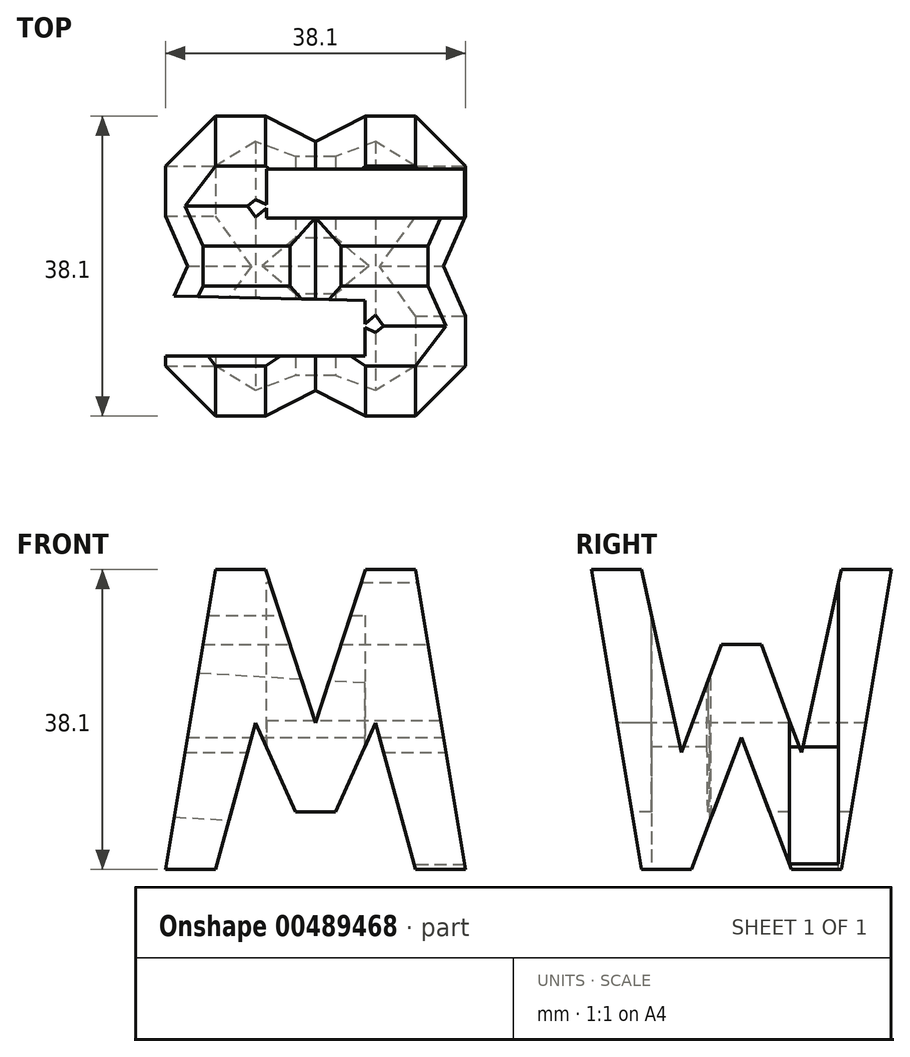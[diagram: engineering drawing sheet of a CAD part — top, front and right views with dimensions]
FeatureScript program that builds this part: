
annotation { "Feature Type Name" : "Feature", "Feature Type Description" : "" }
export const myFeature = defineFeature(function(context is Context, id is Id, definition is map)
    precondition{}
    {
        {
            var Q0;
            Q0=qCreatedBy(makeId("Front.planeOp"),FACE);
            var sketch = newSketch(context, id + "F0", { "sketchPlane" : qUnion([Q0])});
            skLineSegment(sketch, "E0", {"start": v(0, 0) * mm, "end": v(38.1, 0) * mm});
            skLineSegment(sketch, "E1", {"start": v(38.1, 0) * mm, "end": v(38.1, 38.1) * mm});
            skLineSegment(sketch, "E2", {"start": v(38.1, 38.1) * mm, "end": v(0, 38.1) * mm});
            skLineSegment(sketch, "E3", {"start": v(0, 38.1) * mm, "end": v(0, 0) * mm});
            skSolve(sketch);
        }
        {
            var Q0;
            Q0=makeQuery(id+"F0.imprint","IMPRINT",FACE,{"disambiguationData":[TD([[makeQuery(id+"F0.imprint","IMPRINT",EDGE,{"derivedFrom":sQuery(id+"F0.wireOp",EDGE,"E0")}),1.0]])]});
            extrude(context, id + "F1", {"entities" : qUnion([Q0]), "depth" : 38.1 * mm, "offsetDistance" : 25.4 * mm});
        }
        {
            var Q0;
            Q0=qCreatedBy(makeId("Front.planeOp"),FACE);
            cPlane(context, id + "F2", {"entities" : qUnion([Q0]), "cplaneType" : CPlaneType.OFFSET, "offset" : 38.1 * mm, "width" : 152.4 * mm, "height" : 152.4 * mm});
        }
        {
            var Q0;
            Q0=qCreatedBy(makeId("Right.planeOp"),FACE);
            cPlane(context, id + "F3", {"entities" : qUnion([Q0]), "cplaneType" : CPlaneType.OFFSET, "offset" : 38.1 * mm, "width" : 152.4 * mm, "height" : 152.4 * mm});
        }
        {
            var Q0;
            Q0=qCreatedBy(makeId("Top.planeOp"),FACE);
            cPlane(context, id + "F4", {"entities" : qUnion([Q0]), "cplaneType" : CPlaneType.OFFSET, "offset" : 38.1 * mm, "width" : 152.4 * mm, "height" : 152.4 * mm});
        }
        {
            var Q0;
            Q0=qCreatedBy(id+"F3.planeOp",FACE);
            var sketch = newSketch(context, id + "F5", { "sketchPlane" : qUnion([Q0])});
            skLineSegment(sketch, "E4", {"start": v(-38.1, 0) * mm, "end": v(0, 0) * mm});
            skLineSegment(sketch, "E5", {"start": v(0, 0) * mm, "end": v(0, 38.1) * mm});
            skLineSegment(sketch, "E6", {"start": v(-38.1, 0) * mm, "end": v(-38.1, 38.1) * mm});
            skLineSegment(sketch, "E7", {"start": v(-38.1, 38.1) * mm, "end": v(0, 38.1) * mm});
            skLineSegment(sketch, "E8", {"start": v(-38.1, 38.1) * mm, "end": v(-31.75, 0) * mm});
            skLineSegment(sketch, "E9", {"start": v(-31.75, 38.1) * mm, "end": v(-26.67, 14.84) * mm});
            skLineSegment(sketch, "E10", {"start": v(-26.67, 14.84) * mm, "end": v(-21.59, 28.58) * mm});
            skLineSegment(sketch, "E11", {"start": v(-21.59, 28.58) * mm, "end": v(-16.5, 28.58) * mm});
            skLineSegment(sketch, "E12", {"start": v(-16.5, 28.58) * mm, "end": v(-11.43, 14.84) * mm});
            skLineSegment(sketch, "E13", {"start": v(-11.43, 14.84) * mm, "end": v(-6.35, 38.1) * mm});
            skPoint(sketch, "E14.end.orphan", {"position": v(-6.35, 2.22) * mm});
            skLineSegment(sketch, "E15", {"start": v(0, 38.1) * mm, "end": v(-6.35, 0) * mm});
            skPoint(sketch, "E16.end.orphan", {"position": v(-17.5, 15.88) * mm});
            skPoint(sketch, "E17.endSnap0", {"position": v(-19.05, 0) * mm});
            skLineSegment(sketch, "E18", {"start": v(-19.05, 16.79) * mm, "end": v(-12.7, 0) * mm});
            skLineSegment(sketch, "E19", {"start": v(-19.05, 16.79) * mm, "end": v(-25.4, 0) * mm});
            skLineSegment(sketch, "E20.bottom", {"start": v(0, 0) * mm, "end": v(-38.1, 0) * mm});
            skLineSegment(sketch, "E20.top", {"start": v(0, 38.1) * mm, "end": v(-38.1, 38.1) * mm});
            skSolve(sketch);
        }
        {
            var Q0;
            {var subQ1=sQuery(id+"F5.wireOp",EDGE,"E9");Q0=makeQuery(id+"F5.imprint","IMPRINT",FACE,{"disambiguationData":[TD([[makeQuery(id+"F5.imprint","IMPRINT",EDGE,{"derivedFrom":subQ1}),1.0]])]});}
            var Q1;
            {var subQ0=sQuery(id+"F5.wireOp",EDGE,"E8");Q1=makeQuery(id+"F5.imprint","IMPRINT",FACE,{"disambiguationData":[TD([[makeQuery(id+"F5.imprint","IMPRINT",EDGE,{"derivedFrom":subQ0}),-1.0]])]});}
            var Q2;
            {var subQ0=sQuery(id+"F5.wireOp",EDGE,"E18");Q2=makeQuery(id+"F5.imprint","IMPRINT",FACE,{"disambiguationData":[TD([[makeQuery(id+"F5.imprint","IMPRINT",EDGE,{"derivedFrom":subQ0}),-1.0]])]});}
            var Q3;
            {var subQ0=sQuery(id+"F5.wireOp",EDGE,"E15");Q3=makeQuery(id+"F5.imprint","IMPRINT",FACE,{"disambiguationData":[TD([[makeQuery(id+"F5.imprint","IMPRINT",EDGE,{"derivedFrom":subQ0}),1.0]])]});}
            extrude(context, id + "F6", {"entities" : qUnion([Q0, Q1, Q2, Q3]), "operationType" : NewBodyOperationType.REMOVE, "oppositeDirection" : true, "depth" : 38.1 * mm, "offsetDistance" : 25.4 * mm});
        }
        {
            var Q0;
            Q0=qCreatedBy(id+"F2.planeOp",FACE);
            var sketch = newSketch(context, id + "F7", { "sketchPlane" : qUnion([Q0])});
            skLineSegment(sketch, "E21", {"start": v(0, 0) * mm, "end": v(0, 38.1) * mm});
            skLineSegment(sketch, "E22", {"start": v(0, 38.1) * mm, "end": v(38.1, 38.1) * mm});
            skLineSegment(sketch, "E23", {"start": v(38.1, 38.1) * mm, "end": v(38.1, 0) * mm});
            skLineSegment(sketch, "E24", {"start": v(38.1, 0) * mm, "end": v(0, 0) * mm});
            skLineSegment(sketch, "E25", {"start": v(6.35, 38.1) * mm, "end": v(0, 0) * mm});
            skLineSegment(sketch, "E26", {"start": v(12.7, 38.1) * mm, "end": v(19.05, 18.62) * mm});
            skLineSegment(sketch, "E27", {"start": v(19.05, 18.62) * mm, "end": v(25.4, 38.1) * mm});
            skLineSegment(sketch, "E28", {"start": v(31.75, 38.1) * mm, "end": v(38.1, 0) * mm});
            skLineSegment(sketch, "E29", {"start": v(31.75, 0) * mm, "end": v(26.67, 18.62) * mm});
            skLineSegment(sketch, "E30", {"start": v(26.67, 18.62) * mm, "end": v(21.6, 7.31) * mm});
            skLineSegment(sketch, "E31", {"start": v(21.6, 7.31) * mm, "end": v(16.51, 7.31) * mm});
            skLineSegment(sketch, "E32", {"start": v(16.51, 7.31) * mm, "end": v(11.43, 18.62) * mm});
            skLineSegment(sketch, "E33", {"start": v(11.43, 18.62) * mm, "end": v(6.35, 0) * mm});
            skSolve(sketch);
        }
        {
            var Q0;
            {var subQ0=sQuery(id+"F7.wireOp",EDGE,"E26");Q0=makeQuery(id+"F7.imprint","IMPRINT",FACE,{"disambiguationData":[TD([[makeQuery(id+"F7.imprint","IMPRINT",EDGE,{"derivedFrom":subQ0}),1.0]])]});}
            var Q1;
            {var subQ0=sQuery(id+"F7.wireOp",EDGE,"E21");Q1=makeQuery(id+"F7.imprint","IMPRINT",FACE,{"disambiguationData":[TD([[makeQuery(id+"F7.imprint","IMPRINT",EDGE,{"derivedFrom":subQ0}),-1.0]])]});}
            var Q2;
            {var subQ0=sQuery(id+"F7.wireOp",EDGE,"E29");Q2=makeQuery(id+"F7.imprint","IMPRINT",FACE,{"disambiguationData":[TD([[makeQuery(id+"F7.imprint","IMPRINT",EDGE,{"derivedFrom":subQ0}),1.0]])]});}
            var Q3;
            {var subQ0=sQuery(id+"F7.wireOp",EDGE,"E23");Q3=makeQuery(id+"F7.imprint","IMPRINT",FACE,{"disambiguationData":[TD([[makeQuery(id+"F7.imprint","IMPRINT",EDGE,{"derivedFrom":subQ0}),-1.0]])]});}
            extrude(context, id + "F8", {"entities" : qUnion([Q0, Q1, Q2, Q3]), "operationType" : NewBodyOperationType.REMOVE, "oppositeDirection" : true, "depth" : 38.1 * mm, "offsetDistance" : 25.4 * mm});
        }
        {
            var Q0;
            Q0=qCreatedBy(id+"F4.planeOp",FACE);
            var sketch = newSketch(context, id + "F9", { "sketchPlane" : qUnion([Q0])});
            skLineSegment(sketch, "E34", {"start": v(0, 0) * mm, "end": v(0, -46.8) * mm});
            skLineSegment(sketch, "E35", {"start": v(0, -46.8) * mm, "end": v(47.08, -46.8) * mm});
            skLineSegment(sketch, "E36", {"start": v(47.08, -46.8) * mm, "end": v(47.08, 0) * mm});
            skLineSegment(sketch, "E37", {"start": v(47.08, 0) * mm, "end": v(0, 0) * mm});
            skPoint(sketch, "E38.end.orphan", {"position": v(15.78, -7.62) * mm});
            skPoint(sketch, "E39.end.orphan", {"position": v(47.08, -14.97) * mm});
            skLineSegment(sketch, "E40", {"start": v(38.17, -7.62) * mm, "end": v(12.73, -7.62) * mm});
            skLineSegment(sketch, "E41", {"start": v(12.73, -7.62) * mm, "end": v(12.73, -15.24) * mm});
            skLineSegment(sketch, "E42", {"start": v(12.73, -15.24) * mm, "end": v(37.7, -15.24) * mm});
            skPoint(sketch, "E43.end.orphan", {"position": v(0, -38.1) * mm});
            skPoint(sketch, "E44.start.orphan", {"position": v(0, -22.86) * mm});
            skLineSegment(sketch, "E45", {"start": v(0, -22.86) * mm, "end": v(25.3, -23.4) * mm});
            skPoint(sketch, "E45.endSnap0", {"position": v(0, -23.4) * mm});
            skLineSegment(sketch, "E46", {"start": v(25.3, -23.4) * mm, "end": v(25.3, -30.48) * mm});
            skLineSegment(sketch, "E47", {"start": v(25.3, -30.48) * mm, "end": v(0, -30.48) * mm});
            skSolve(sketch);
        }
        {
            var Q0;
            {var subQ0=sQuery(id+"F9.wireOp",EDGE,"E45");Q0=makeQuery(id+"F9.imprint","IMPRINT",FACE,{"disambiguationData":[TD([[makeQuery(id+"F9.imprint","IMPRINT",EDGE,{"derivedFrom":subQ0}),-1.0]])]});}
            extrude(context, id + "F10", {"entities" : qUnion([Q0]), "operationType" : NewBodyOperationType.REMOVE, "oppositeDirection" : true, "depth" : 38.1 * mm, "offsetDistance" : 25.4 * mm});
        }
        {
            var Q0;
            Q0=qCreatedBy(id+"F4.planeOp",FACE);
            var sketch = newSketch(context, id + "F11", { "sketchPlane" : qUnion([Q0])});
            skLineSegment(sketch, "E48", {"start": v(0, 0) * mm, "end": v(0, -37.96) * mm});
            skLineSegment(sketch, "E49", {"start": v(0, -37.96) * mm, "end": v(37.98, -37.96) * mm});
            skLineSegment(sketch, "E50", {"start": v(37.98, -37.96) * mm, "end": v(37.98, 0) * mm});
            skLineSegment(sketch, "E51", {"start": v(37.98, 0) * mm, "end": v(0, 0) * mm});
            skLineSegment(sketch, "E52", {"start": v(37.98, -6.7) * mm, "end": v(12.8, -6.7) * mm});
            skLineSegment(sketch, "E53", {"start": v(12.8, -6.7) * mm, "end": v(12.8, -12.93) * mm});
            skLineSegment(sketch, "E54", {"start": v(12.8, -12.93) * mm, "end": v(37.98, -12.93) * mm});
            skSolve(sketch);
        }
        {
            var Q0;
            {var subQ0=sQuery(id+"F11.wireOp",EDGE,"E52");Q0=makeQuery(id+"F11.imprint","IMPRINT",FACE,{"disambiguationData":[TD([[makeQuery(id+"F11.imprint","IMPRINT",EDGE,{"derivedFrom":subQ0}),1.0]])]});}
            extrude(context, id + "F12", {"entities" : qUnion([Q0]), "operationType" : NewBodyOperationType.REMOVE, "oppositeDirection" : true, "depth" : 38.1 * mm, "offsetDistance" : 25.4 * mm});
        }
    });
